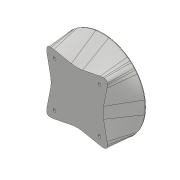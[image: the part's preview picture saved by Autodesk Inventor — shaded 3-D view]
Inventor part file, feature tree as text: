
AUTODESK INVENTOR PART (.ipt)
format: ipt  version: 2018 (Build 220112000, 112)  size: 2,089,984 bytes
history: native  units: mm
features: sketch x39, projected_geometry x35, extrude x32, fillet x9, hole x5, chamfer x5, other x2, mirror x1, revolve x1, shell x1, pattern_circular x1, plane x1, loft x1
ambient origin geometry x8: Origin, YZ Plane, XZ Plane, XY Plane, X Axis, Y Axis, Z Axis, Center Point
bodies: Solid1 (feature_tree)
feature tree (133):
  extrude  "Extrusion1"  Depth=45.0mm
  extrude  "Extrusion2"  Depth=2.25mm
  hole  "Hole1"  [1 undecoded]
  hole  "Hole2"  [1 undecoded]
  fillet  "Fillet1"  Radius=14.0mm
  extrude  "Extrusion3"  Depth=18.5mm
  extrude  "Extrusion4"  Depth=20.5mm
  extrude  "Extrusion5"  Depth=2.195mm
  extrude  "Extrusion6"  Depth=20.5mm
  hole  "Hole3"  [1 undecoded]
  extrude  "Extrusion7"  Depth=0.5mm
  extrude  "Extrusion8"  Depth=5.0mm TaperAngle=0.0deg
  extrude  "Extrusion9"  Depth=24.5mm
  extrude  "Extrusion10"  Depth=10.0mm
  extrude  "Extrusion11"  Depth=14.5mm
  extrude  "Extrusion12"  Depth=14.5mm
  extrude  "Extrusion13"  Depth=5.0mm
  extrude  "Extrusion14"  Depth=2.25mm
  extrude  "Extrusion15"  Depth=5.0mm
  extrude  "Extrusion16"  Depth=9.0mm
  extrude  "Extrusion17"  Depth=4.0mm
  chamfer  "Chamfer1"  Distance=1.0mm
  fillet  "Fillet7"  Radius=20.7mm
  fillet  "Fillet8"  Radius=32.0mm
  mirror  "Mirror1"
  extrude  "Extrusion18"  Depth=1.0mm TaperAngle=0.0deg
  extrude  "Extrusion19"  Depth=8.0mm
  extrude  "Extrusion20"  Depth=0.2mm TaperAngle=0.0deg
  extrude  "Extrusion21"  Depth=0.5mm TaperAngle=0.0deg
  extrude  "Extrusion22"  Depth=3.0mm TaperAngle=0.0deg
  extrude  "Extrusion23"  Depth=0.2mm TaperAngle=0.0deg
  extrude  "Extrusion24"  Depth=2.5mm TaperAngle=45.0deg
  sketch  "Sketch35"  dims[d91=8.0mm d92=0.0mm d93=3.0mm d94=0.0mm]
  other  "Work Axis1"
  revolve  "Revolution1"  [1 undecoded]
  extrude  "Extrusion25"  Depth=4.0mm TaperAngle=0.0deg
  extrude  "Extrusion26"  Depth=19.2mm TaperAngle=0.0deg
  shell  "Shell1"  Thickness=52.1mm
  extrude  "Extrusion27"  Depth=9.0mm
  extrude  "Extrusion28"  Depth=25.0mm
  chamfer  "Chamfer4"  Distance=6.9mm
  chamfer  "Chamfer5"  Distance=2.5mm
  extrude  "Extrusion29"  Depth=5.0mm
  pattern_circular  "Circular Pattern1"  Angle=90.0deg  [1 undecoded]
  fillet  "Fillet11"  Radius=5.0mm
  fillet  "Fillet12"  Radius=105.0mm
  fillet  "Fillet13"  Radius=105.0mm
  fillet  "Fillet14"  Radius=5.0mm
  chamfer  "Chamfer6"  Distance=12.8mm
  hole  "Hole6"  [1 undecoded]
  extrude  "Extrusion30"  Depth=12.8mm
  fillet  "Fillet15"  Radius=12.8mm
  extrude  "Extrusion31"  Depth=20.0mm
  plane  "Work Plane1"
  loft  "Loft1"
  hole  "Hole8"  [1 undecoded]
  extrude  "Extrusion35"  Depth=6.0mm
  chamfer  "Chamfer7"  Distance=40.0mm
  fillet  "Fillet20"  Radius=8.0mm
  sketch  "Sketch1"  dims[d0=24.5mm d1=45.0mm]
  sketch  "Sketch2"  dims[d2=1.95mm d3=0.0mm d4=2.25mm]
  projected_geometry  "Projected Loop1"
  sketch  "Sketch3"  dims[d5=20.0mm d6=2.25mm]
  projected_geometry  "Projected Loop2"
  sketch  "Sketch4"  dims[d7=5.25mm d8=5.25mm d9=14.0mm]
  projected_geometry  "Projected Loop3"
  sketch  "Sketch5"  dims[d10=5.25mm d11=18.5mm]
  projected_geometry  "Projected Loop4"
  sketch  "Sketch6"  dims[d12=10.0mm d13=0.0mm d14=20.5mm]
  projected_geometry  "Projected Loop5"
  sketch  "Sketch7"  dims[d15=2.0mm d16=2.195mm]
  projected_geometry  "Projected Loop6"
  sketch  "Sketch8"  dims[d17=2.0mm]
  projected_geometry  "Projected Loop7"
  sketch  "Sketch9"  dims[d18=2.4mm d19=6.0mm d20=4.4mm d21=2.0mm d22=90.0deg d23=8.0mm d24=20.594885mm d25=20.5mm]
  projected_geometry  "Projected Loop8"
  projected_geometry  "Projected Loop9"
  sketch  "Sketch10"  dims[d26=26.65mm d27=2.0mm]
  projected_geometry  "Projected Loop10"
  projected_geometry  "Projected Loop11"
  sketch  "Sketch11"  dims[d28=2.0mm]
  projected_geometry  "Projected Loop12"
  sketch  "Sketch12"  dims[d29=2.4mm d30=6.0mm d31=4.4mm d32=2.0mm d33=90.0deg d34=8.0mm d35=20.594885mm d36=0.5mm]
  sketch  "Sketch13"  dims[d37=18.0mm d38=5.0mm d39=0.0mm]
  sketch  "Sketch14"  dims[d41=10.0mm d42=0.0mm d43=24.5mm]
  projected_geometry  "Projected Loop13"
  sketch  "Sketch15"  dims[d44=1.15mm d45=0.0mm d46=10.0mm]
  sketch  "Sketch16"  dims[d47=21.0mm d48=14.5mm]
  projected_geometry  "Projected Loop14"
  sketch  "Sketch17"  dims[d49=20.0mm d50=14.5mm]
  projected_geometry  "Projected Loop15"
  sketch  "Sketch18"  dims[d51=24.5mm d52=5.0mm]
  projected_geometry  "Projected Loop16"
  sketch  "Sketch19"  dims[d53=5.0mm d54=2.25mm]
  projected_geometry  "Projected Loop17"
  sketch  "Sketch20"  dims[d55=2.25mm d56=5.0mm]
  projected_geometry  "Projected Loop18"
  sketch  "Sketch22"  dims[d57=5.0mm d58=9.0mm]
  sketch  "Sketch25"  dims[d59=14.75mm d60=4.0mm d61=1.0mm d62=0.0mm d63=20.7mm]
  sketch  "Sketch27"  dims[d64=2.4mm d65=6.0mm d66=4.4mm d67=2.0mm d68=90.0deg d69=8.0mm d70=20.594885mm d72=32.0mm]
  projected_geometry  "Projected Loop22"
  sketch  "Sketch28"  dims[d73=5.0mm d74=0.0mm d75=1.0mm d76=0.0mm]
  projected_geometry  "Projected Loop23"
  sketch  "Sketch29"  dims[d77=12.25mm d78=0.0mm d80=8.0mm]
  projected_geometry  "Projected Loop24"
  sketch  "Sketch30"  dims[d81=4.5mm d82=0.0mm d84=0.2mm d85=0.0mm]
  projected_geometry  "Projected Loop25"
  sketch  "Sketch33"  dims[d86=21.0mm d87=0.5mm d88=0.0mm]
  projected_geometry  "Projected Loop26"
  sketch  "Sketch36"  dims[d95=5.0mm d96=0.0mm d98=0.2mm d99=0.0mm]
  projected_geometry  "Projected Loop27"
  sketch  "Sketch37"  dims[d100=0.2mm d101=0.0mm d102=2.5mm d103=2.0mm d104=45.0deg]
  projected_geometry  "Projected Loop28"
  sketch  "Sketch38"  dims[d105=1.5mm d114=0.5mm]
  projected_geometry  "Projected Loop29"
  projected_geometry  "Projected Loop30"
  projected_geometry  "Projected Loop31"
  projected_geometry  "Projected Loop32"
  sketch  "Sketch39"  dims[d115=22.55mm d116=0.0mm d128=4.0mm d129=0.0mm]
  projected_geometry  "Projected Loop33"
  projected_geometry  "Projected Loop34"
  sketch  "Sketch40"  dims[d130=4.0mm d131=0.0mm d132=19.2mm d133=0.0mm d134=52.1mm]
  projected_geometry  "Projected Loop35"
  sketch  "Sketch41"  dims[d135=6.8mm d136=0.0mm d137=9.0mm]
  projected_geometry  "Projected Loop36"
  sketch  "Sketch42"  dims[d138=9.0mm d139=25.0mm d140=6.9mm d141=0.0mm]
  sketch  "Sketch43"  dims[d142=5.2mm]
  projected_geometry  "Projected Loop37"
  sketch  "Sketch49"  dims[d143=5.2mm]
  other  "Edges1"
  sketch  "Sketch50"  dims[d144=5.2mm]
  sketch  "Sketch51"  dims[d145=5.2mm d146=2.5mm d147=0.0mm d148=5.0mm d149=90.0deg d150=5.0mm d151=105.0mm d152=105.0mm d153=5.0mm d154=0.0mm d156=12.8mm d157=12.8mm d158=12.8mm d159=12.8mm d160=20.0mm d161=20.0mm d162=20.0mm d163=6.0mm d164=40.0mm d165=0.0mm d166=8.0mm d167=40.0mm d168=0.0mm d169=40.0mm d170=0.0mm d178=5.1mm d179=2.45mm d180=45.0deg d181=4.1mm d182=2.45mm d183=45.0deg d184=10.0mm d185=10.0mm d186=40.0mm d187=0.0mm d188=40.0mm d189=360.0deg d191=5.1mm d192=25.0mm d193=50.0mm d194=50.0mm d195=5.0mm d196=2.0mm d197=45.0deg d198=110.0mm d199=77.781746mm d200=77.781746mm d201=6.4mm d202=6.0mm d203=12.6mm d204=2.0mm d205=90.0deg d206=8.0mm d207=20.594885mm d208=11.0mm d209=11.0mm d210=11.0mm d211=11.0mm d212=45.0mm d213=0.0mm d214=1.0mm d215=2.0mm d216=0.0mm d236=45.0mm d237=150.0mm d238=0.0mm d239=90.0deg d240=0.0mm d241=90.0deg d242=4.917mm d243=60.0mm d244=4.0mm d245=2.0mm d246=90.0deg d247=17.1mm d248=20.594885mm d249=45.0mm d250=0.0mm d251=1.0mm d252=2.0mm d253=45.0deg d254=1.0mm]
  projected_geometry  "Project Cut Edges1"
note: 7 required parameter values undecoded (feature->parameter linkage not recoverable at this tier; creation-order binding heuristic only, values carry confidence <= 0.55)